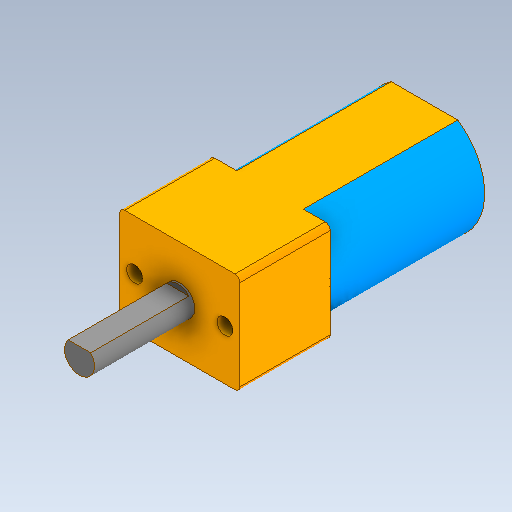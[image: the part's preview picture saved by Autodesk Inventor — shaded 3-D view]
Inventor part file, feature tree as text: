
AUTODESK INVENTOR PART (.ipt)
format: ipt  version: 2020 (Build 240168000, 168)  size: 171,008 bytes
history: native  units: mm
features: extrude x6, sketch x4, projected_geometry x2, fillet x1
ambient origin geometry x8: Origin, YZ Plane, XZ Plane, XY Plane, X Axis, Y Axis, Z Axis, Center Point
bodies: Solid1 (feature_tree)
feature tree (13):
  sketch  "Sketch1"  dims[d0=10.0mm d1=12.0mm]
  extrude  "Extrusion1"  Depth=12.0mm
  extrude  "Extrusion2"  Depth=9.0mm
  extrude  "Extrusion3"  Depth=9.0mm TaperAngle=0.0deg
  extrude  "Extrusion4"  Depth=10.0mm TaperAngle=0.0deg
  extrude  "Extrusion5"  Depth=0.5mm
  extrude  "Extrusion6"  Depth=9.8mm TaperAngle=0.0deg
  fillet  "Fillet1"  Radius=15.4mm
  sketch  "Sketch2"  dims[d2=9.0mm d3=1.6mm]
  projected_geometry  "Projected Loop1"
  sketch  "Sketch3"  dims[d4=3.0mm d5=9.0mm d6=0.0mm]
  projected_geometry  "Projected Loop2"
  sketch  "Sketch4"  dims[d7=0.0mm d8=0.0mm d9=10.0mm d10=0.0mm d11=1.0mm d12=9.8mm d13=0.0mm d14=15.4mm d15=0.0mm d16=5.0mm d17=0.8mm d18=0.0mm d19=0.5mm]
